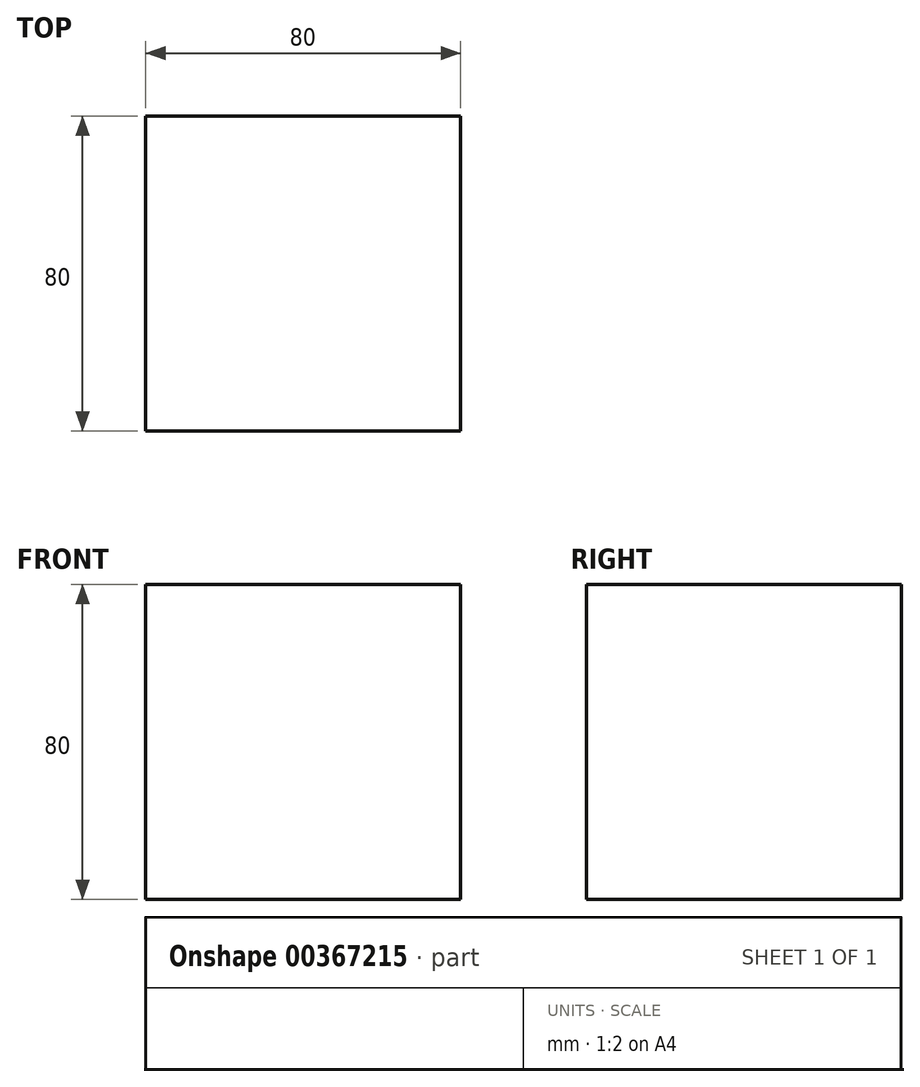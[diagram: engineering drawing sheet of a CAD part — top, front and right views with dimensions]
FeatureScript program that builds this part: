
annotation { "Feature Type Name" : "Feature", "Feature Type Description" : "" }
export const myFeature = defineFeature(function(context is Context, id is Id, definition is map)
    precondition{}
    {
        {
            var Q0;
            Q0=qCreatedBy(makeId("Top.planeOp"),FACE);
            var sketch = newSketch(context, id + "F0", { "sketchPlane" : qUnion([Q0])});
            skLineSegment(sketch, "E0.bottom", {"start": v(40, -40) * mm, "end": v(-40, -40) * mm});
            skLineSegment(sketch, "E0.top", {"start": v(40, 40) * mm, "end": v(-40, 40) * mm});
            skLineSegment(sketch, "E0.left", {"start": v(40, -40) * mm, "end": v(40, 40) * mm});
            skLineSegment(sketch, "E0.right", {"start": v(-40, -40) * mm, "end": v(-40, 40) * mm});
            skPoint(sketch, "E0.middle", {"position": v(0, 0) * mm});
            skSolve(sketch);
        }
        {
            var Q0;
            Q0=makeQuery(id+"F0.imprint","IMPRINT",FACE,{"disambiguationData":[TD([[makeQuery(id+"F0.imprint","IMPRINT",EDGE,{"derivedFrom":sQuery(id+"F0.wireOp",EDGE,"E0.bottom")}),-1.0]])]});
            extrude(context, id + "F1", {"entities" : qUnion([Q0]), "depth" : 80 * mm});
        }
    });
